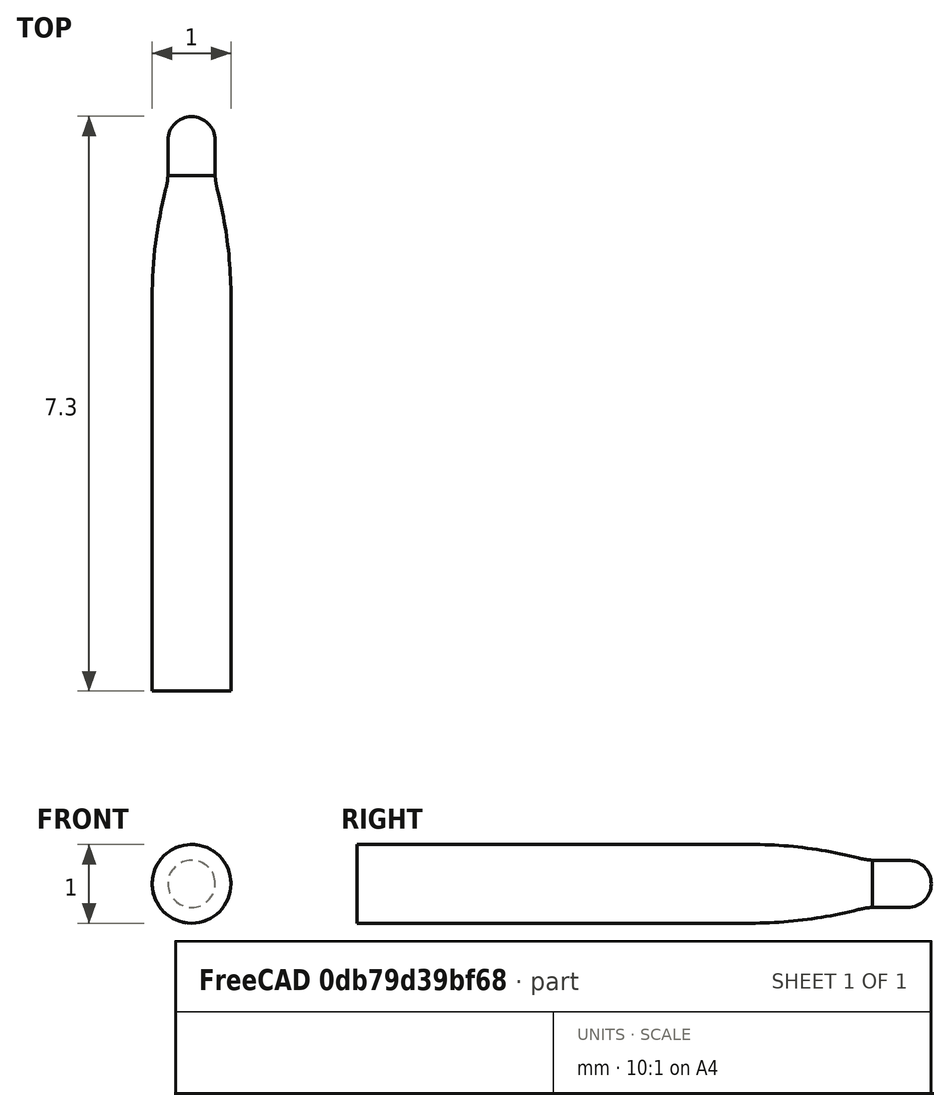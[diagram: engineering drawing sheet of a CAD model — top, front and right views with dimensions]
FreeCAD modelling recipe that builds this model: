
FCSTD DOCUMENT  (FreeCAD 0.16R6712 (Git))
Label: colonbulb
License: All rights reserved
LicenseURL: http://en.wikipedia.org/wiki/All_rights_reserved
objects: Sketcher::SketchObject×1, PartDesign::Revolution×1, Mesh::Feature×1
note: 3 computed .brp shape members not serialized (recipe doc carries the construction recipe); baked Part::Feature solids carry a one-line shape summary decoded from their .brp

FEATURE [Sketcher::SketchObject] Sketch
  sketch-geometry (7):
    g0: LineSegment StartX=-0.5 StartY=3 StartZ=0 EndX=-0.5 EndY=-2 EndZ=0
    g1: ArcOfCircle CenterX=5.033 CenterY=3 CenterZ=0 NormalX=0 NormalY=0 NormalZ=1 Radius=5.533 StartAngle=2.89076 EndAngle=3.14159
    g2: LineSegment StartX=-0.5 StartY=-2 StartZ=0 EndX=0 EndY=-2 EndZ=0
    g3: ArcOfCircle CenterX=-1.20415 CenterY=4.59815 CenterZ=0 NormalX=0 NormalY=0 NormalZ=1 Radius=0.905645 StartAngle=6.03234 EndAngle=6.22576
    g4: LineSegment StartX=0 StartY=5.29618 StartZ=0 EndX=0 EndY=-2 EndZ=0
    g5: LineSegment StartX=-0.3 StartY=4.54618 StartZ=0 EndX=-0.3 EndY=4.99618 EndZ=0
    g6: ArcOfCircle CenterX=0 CenterY=4.99618 CenterZ=0 NormalX=0 NormalY=0 NormalZ=1 Radius=0.3 StartAngle=1.5708 EndAngle=3.14159
  constraints (22):
    c: Vertical(g0)
    c: DistanceX(g-2,g0) = -0.5
    c: Coincident(g1,g0)
    c: Tangent(g1,g0)
    c: Horizontal(g2)
    c: PointOnObject(g2,g-2)
    c: Coincident(g3,g1)
    c: Tangent(g1,g3)
    c: DistanceY(g-1,g2) = -2
    c: Coincident(g4,g2)
    c: Coincident(g5,g3)
    c: Vertical(g5)
    c: PointOnObject(g6,g4)
    c: Coincident(g6,g5)
    c: PointOnObject(g6,g4)
    c: Tangent(g5,g6)
    c: Radius(g6) = 0.3
    c: Coincident(g4,g6)
    c: PointOnObject(g4,g-2)
    c: Distance(g0,g2) = 5
    c: DistanceY(g3,g4) = 0.75
    c: Coincident(g2,g0)
FEATURE [PartDesign::Revolution] Revolution
  Angle = 360
  Axis = (0,1,0)
  Base = (0,0,0)
  ReferenceAxis = -> Sketch [V_Axis]
  Sketch = -> Sketch
FEATURE [Mesh::Feature] Mesh  label="Revolution (Meshed)"
